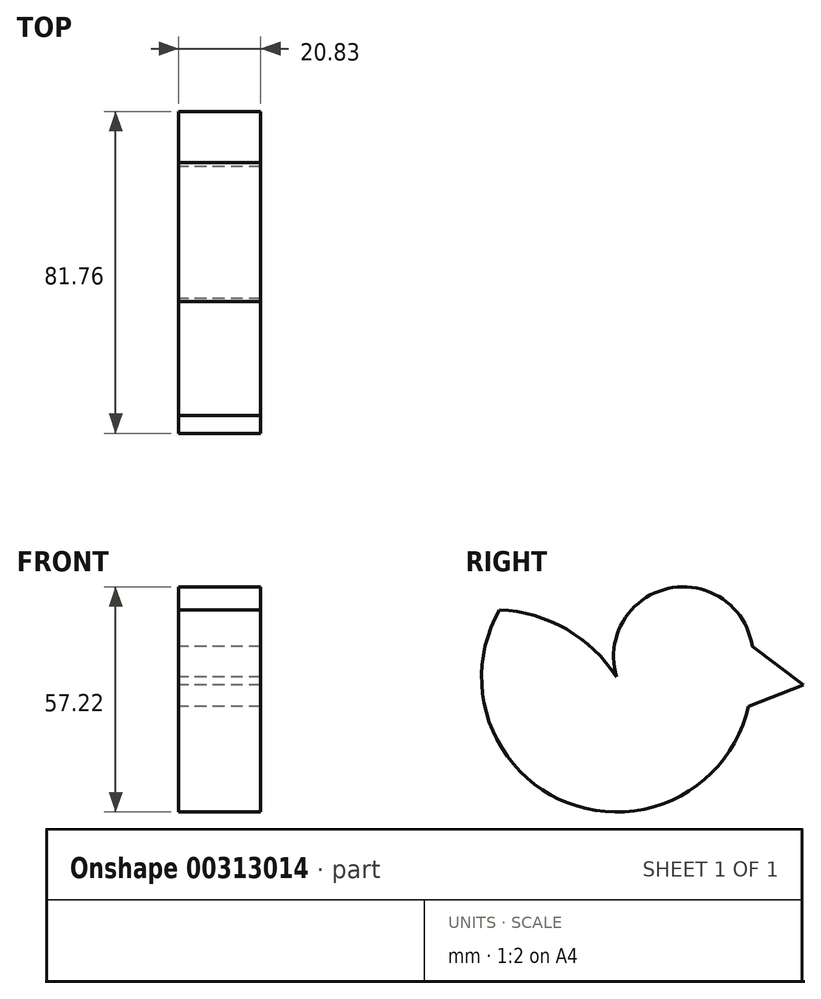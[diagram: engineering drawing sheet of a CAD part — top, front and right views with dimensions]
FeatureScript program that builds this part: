
annotation { "Feature Type Name" : "Feature", "Feature Type Description" : "" }
export const myFeature = defineFeature(function(context is Context, id is Id, definition is map)
    precondition{}
    {
        {
            var Q0;
            Q0=qCreatedBy(makeId("Right.planeOp"),FACE);
            var sketch = newSketch(context, id + "F0", { "sketchPlane" : qUnion([Q0])});
            skArc(sketch, "E0", {"start": v(-68.63, 51.64) * mm, "mid": v(-46.96, 1.22) * mm, "end": v(-4.62, 36.13) * mm});
            skArc(sketch, "E1", {"start": v(-4.62, 36.13) * mm, "mid": v(-22.76, 57.46) * mm, "end": v(-38.88, 34.56) * mm});
            skArc(sketch, "E2", {"start": v(-38.88, 34.56) * mm, "mid": v(-51.67, 46.72) * mm, "end": v(-68.63, 51.64) * mm});
            skLineSegment(sketch, "E3", {"start": v(-4.43, 42.35) * mm, "end": v(8.58, 32.5) * mm});
            skLineSegment(sketch, "E4", {"start": v(8.58, 32.5) * mm, "end": v(-5.4, 27.14) * mm});
            skLineSegment(sketch, "E5", {"start": v(-5.4, 27.14) * mm, "end": v(8.58, 32.5) * mm});
            skLineSegment(sketch, "E6", {"start": v(-62.24, 9.44) * mm, "end": v(-73.25, -3.13) * mm});
            skLineSegment(sketch, "E7", {"start": v(-73.25, -3.13) * mm, "end": v(-68.62, -7.18) * mm});
            skLineSegment(sketch, "E8", {"start": v(-68.62, -7.18) * mm, "end": v(-73.25, -3.13) * mm});
            skLineSegment(sketch, "E9", {"start": v(-73.25, -3.13) * mm, "end": v(-77.17, -3.5) * mm});
            skLineSegment(sketch, "E10", {"start": v(-75.23, -4.45) * mm, "end": v(-77.17, -3.5) * mm});
            skLineSegment(sketch, "E11", {"start": v(-38.94, 0.26) * mm, "end": v(-36.3, -17) * mm});
            skLineSegment(sketch, "E12", {"start": v(-36.3, -17) * mm, "end": v(-45.07, -18.34) * mm});
            skLineSegment(sketch, "E13", {"start": v(-45.07, -18.34) * mm, "end": v(-36.3, -17) * mm});
            skLineSegment(sketch, "E14", {"start": v(-36.3, -17) * mm, "end": v(-32.5, -20.3) * mm});
            skSolve(sketch);
        }
        {
            var Q0;
            Q0 = qSketchRegion(id + "F0", true);
            extrude(context, id + "F1", {"entities" : qUnion([Q0]), "depth" : 20.83 * mm});
        }
    });
